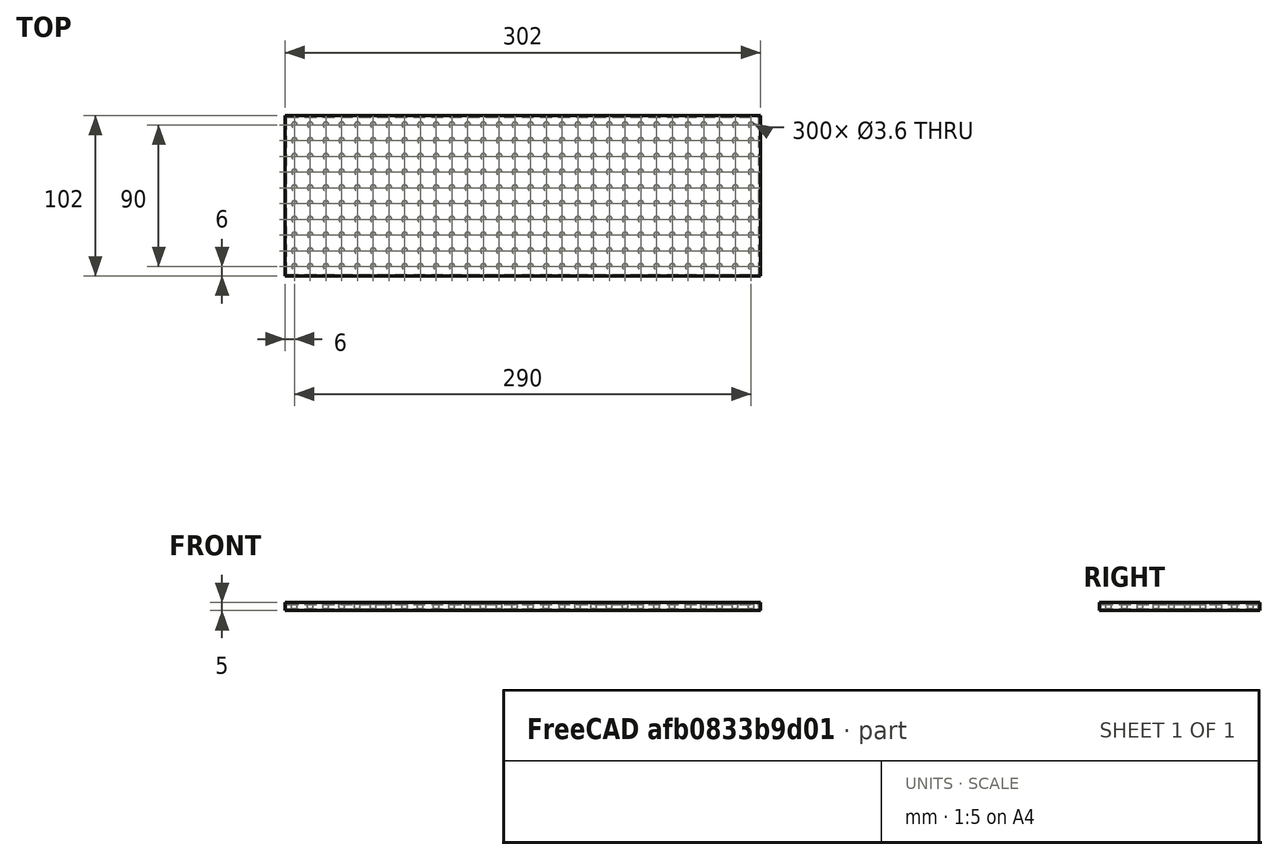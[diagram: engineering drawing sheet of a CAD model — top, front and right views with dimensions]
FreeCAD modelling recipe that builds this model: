
FCSTD DOCUMENT  (FreeCAD 0.18.4R)
Label: hole_plate
License: All rights reserved
LicenseURL: http://en.wikipedia.org/wiki/All_rights_reserved
objects: Path::FeaturePython×4, Part::FeaturePython×3, Part::Box×1, Spreadsheet::Sheet×1, Part::Cylinder×1, Part::Cut×1, App::FeaturePython×1, App::DocumentObjectGroup×1, Path::FeatureCompoundPython×1
note: 7 computed .brp shape members not serialized (recipe doc carries the construction recipe); baked Part::Feature solids carry a one-line shape summary decoded from their .brp

FEATURE [Part::Box] Box  label="hole plate cube"
  AttacherType = Attacher::AttachEngine3D
  Height = 3
  Length = 300
  Width = 100
  expr: Length = p.plate_x
  expr: Width = p.plate_y
FEATURE [Spreadsheet::Sheet] Spreadsheet  label="p"
  cells = A1=hole_r; B1(hole_r)=1.8; A2=plate_hole_dist; B2(plate_hole_dist)=10; A3=plate_x; B3(plate_x)=300; A4=plate_y; B4(plate_y)=100
FEATURE [Part::Cylinder] Cylinder  label="the hole"
  Angle = 360
  AttacherType = Attacher::AttachEngine3D
  Height = 10
  Radius = 1.8
  expr: Radius = p.hole_r
FEATURE [Part::FeaturePython] Array  label="hole array"  # Draft array (typed FeaturePython)
  Angle = 360
  ArrayType = 0
  Axis = (0,0,1)
  Base = -> Cylinder
  Center = (0,0,0)
  Fuse = false
  IntervalAxis = (0,0,0)
  IntervalX = (10,0,0)
  IntervalY = (0,10,0)
  IntervalZ = (0,0,1)
  NumberPolar = 1
  NumberX = 30
  NumberY = 10
  NumberZ = 1
  Placement = pos=(5,5,0) rot=(0,0,1;0rad)
  expr: Placement.Base.y = p.plate_hole_dist / 2
  expr: Placement.Base.x = p.plate_hole_dist / 2
  expr: IntervalX.x = p.plate_hole_dist
  expr: NumberY = floor(p.plate_y / p.plate_hole_dist)
  expr: NumberX = floor(p.plate_x / p.plate_hole_dist)
FEATURE [Part::Cut] Cut  label="hole plate cut"
  Base = -> Box
  Tool = -> Array
FEATURE [App::FeaturePython] SetupSheet  # Path/CAM operation (typed FeaturePython)
  ClearanceHeightExpression = OpStockZMax+SetupSheet.ClearanceHeightOffset
  ClearanceHeightOffset = 0
  FinalDepthExpression = OpFinalDepth
  HorizRapid = 100
  SafeHeightExpression = OpStockZMax+SetupSheet.SafeHeightOffset
  SafeHeightOffset = 0
  StartDepthExpression = OpStartDepth
  StepDownExpression = OpToolDiameter
  VertRapid = 100
FEATURE [Part::FeaturePython] Clone  label="Model-hole plate cut"  # Draft clone (typed FeaturePython)
  AttacherType = Attacher::AttachEngine3D
  Fuse = false
  Objects = -> [Cut]
  PathResource = Model
  Scale = (1,1,1)
FEATURE [App::DocumentObjectGroup] Model
  Group = -> [Clone]
FEATURE [Path::FeaturePython] T3__laser  label="T3: laser"  # Path/CAM operation (typed FeaturePython)
  HorizFeed = 0.5
  HorizRapid = 100
  SpindleDir = 0
  SpindleSpeed = 1000
  ToolNumber = 3
  VertFeed = 0.5
  VertRapid = 100
  expr: VertRapid = SetupSheet.VertRapid
  expr: HorizRapid = SetupSheet.HorizRapid
FEATURE [Part::FeaturePython] Stock  # WARN: FeaturePython — macro-defined, semantics opaque (R4)
  Base = -> Model
  ExtXneg = 1
  ExtXpos = 1
  ExtYneg = 1
  ExtYpos = 1
  ExtZneg = 1
  ExtZpos = 1
  StockType = FromBase
FEATURE [Path::FeaturePython] Contour  # Path/CAM operation (typed FeaturePython)
  Active = true
  AreaParams:
    Tolerance = 1e-07
    FitArcs = True
    Simplify = False
    CleanDistance = 0.0
    Accuracy = 0.01
    Unit = 1.0
    MinArcPoints = 4
    MaxArcPoints = 100
    ClipperScale = 10000000.0
    Fill = 0
    Coplanar = 2
    Reorient = True
    Outline = False
    Explode = False
    OpenMode = 0
    Deflection = 0.01
    SubjectFill = 0
    ClipFill = 0
    Offset = 0.1
    ExtraPass = 0
    Stepover = 0.0
    LastStepover = 0.0
    JoinType = 0
    EndType = 0
    MiterLimit = 2.0
    RoundPrecision = 0.0
    PocketMode = 0
    ToolRadius = 1.0
    PocketExtraOffset = 0.0
    PocketStepover = 0.0
    PocketLastStepover = 0.0
    FromCenter = False
    Angle = 45.0
    AngleShift = 0.0
    Shift = 0.0
    Thicken = False
    SectionCount = -1
    Stepdown = 1.0
    SectionOffset = 0.0
    SectionTolerance = 1e-06
    SectionMode = 2
    Project = False
  ClearanceHeight = 1
  Direction = 0
  FinalDepth = 0
  JoinType = 0
  MiterLimit = 0.1
  OffsetExtra = 0
  OpFinalDepth = -1
  OpStartDepth = 4
  OpStockZMax = 4
  OpStockZMin = -1
  OpToolDiameter = 0.2
  PathParams = {'orientation': 1, 'feedrate': 0.5, 'feedrate_v': 0.5, 'verbose': True, 'resume_height': 1.0, 'retraction': 1.0, 'return_end': True, 'preamble': False}
  SafeHeight = 1
  Side = 0
  StartDepth = 0.1
  StartPoint = (0,0,0)
  StepDown = 0.2
  ToolController = -> T3__laser
  UseComp = true
  UseStartPoint = false
FEATURE [Path::FeaturePython] Engrave  # Path/CAM operation (typed FeaturePython)
  Active = true
  Base = -> [Clone]
  ClearanceHeight = 1
  FinalDepth = 0
  OpFinalDepth = 2.8
  OpStartDepth = 3
  OpStockZMax = 4
  OpStockZMin = -1
  OpToolDiameter = 0.2
  SafeHeight = 1
  StartDepth = 4.1
  StartVertex = 0
  StepDown = 0.2
  ToolController = -> T3__laser
  expr: StepDown = OpToolDiameter
FEATURE [Path::FeatureCompoundPython] Operations  # Path/CAM operation (typed FeaturePython)
  Group = -> [Contour,Engrave]
  UsePlacements = false
FEATURE [Path::FeaturePython] Job  label="hole plate job"  # Path/CAM operation (typed FeaturePython)
  GeometryTolerance = 0.01
  Model = -> Model
  Operations = -> Operations
  PostProcessor = 1
  PostProcessorOutputFile = <userpath>/work/roborep/freecad/hole_plate/hole_plate.gcode
  SetupSheet = -> SetupSheet
  Stock = -> Stock
  ToolController = -> [T3__laser]
